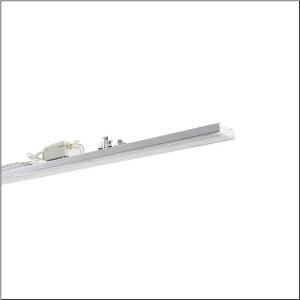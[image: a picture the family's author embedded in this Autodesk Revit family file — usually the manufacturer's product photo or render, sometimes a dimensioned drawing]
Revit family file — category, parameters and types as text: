
# Revit family: licross_21_recessed_mo_52te12dn4axg3s
name_source: partatom
category: Lighting Fixtures
units: mm (PartAtom-declared; Revit-internal decimal feet)

## family parameters
Cut with Voids When Loaded = No
Host = Face
Light Source = No
Part Type = Normal
Room Calculation Point = No
Round Connector Dimension = Use Diameter
Shared = No

## types (1)
- --- (1 x LED, 950 lm, 6.7 W, 4000K)
    Apparent Load = 7 VA
    CIE Flux Codes = 72 92 99 100 100
    Color Rendering = 80
    Color Temperature = 4000K
    Default Elevation = 1800 mm
    Description = Licross 21 Recessed MO, luminaire insert, of sheet steel, galvanised, coil coated, white, length: 1.500mm, width: 66mm, height: 67mm, LED rated luminous flux: 10.280lm, light colour: 840, SDCM (Standard Deviation of Colour Matching)MacAdam ≤ 3 SDCM (initial), control gear: DALI 2 (for two DALI lines), with plug, 6-pole, with phase selection, for trunking rail, 14-core, mains connection: 220..240V, AC, 50/60Hz, rated input power: 62W, internal wiring halogen-free, for emergency light function, for trunking rail, 14-core, converter,control gear: single battery element, battery: LiFePO4, 9Ah, primary optical cover: cover, of PMMA, light emission: direct distribution, primary light characteristic: symmetric, protection rating (complete): IP54, insulation class (complete): insulation class I (protective earthing), certification: CE, UKCA, protection symbol: D if used in an environment with non-conductive dust loads with corresponding accessories, impact resistance: IK06, permissible ambient temperature for indoor applications: +5..+35°C, standard: EN 60598-2-22, LABS conformity tested according to VDMA 24364:2018-05, reducing of maximum allowable ambient temperature of 5°C with ceiling mounting, corresponds to IFS (International Featured Standards) requirements for safety and quality in the food industry, The light source and the operating device comply with the requirements of the Ecodesign Regulation (EU) 2019/2020 and are replaceable in accordance with this regulation, packaging unit: 1 piece
    Height = 58 mm
    Lamp = 1 x LED
    Lamp Light Flux = 950 lm
    Lamp Power = 6.7 W
    Lamp count = 1
    Length = 1500 mm
    Luminous efficacy = 142 lm/W
    Manufacturer = Siteco
    ModVariant = No
    Model = 52TE12DN4AXG3S
    Mounting Place = Ceiling
    Mounting Type = Pendant
    Number of Poles = 1
    OnlyDefault = Yes
    Power Factor = 1
    Product Name = Licross 21 Recessed MO
    Product group = luminaire insert | ceiling pendant
    ProductGroupID = 901
    Protection Class = Protection class I
    Protection Degree = IP 54
    RLX_Detail_Level = 1
    RLX_Emergency_Light_Flux = 0 lm
    RLX_Emergency_Type = 0
    RLX_Emergency_Type_DB = No
    RlxData = <blob elided: 25297 chars, md5=afd6981c>
    Socket = socket
    Standby Power = 0 W
    System Light Flux = 950 lm
    System Power = 7 W
    Type Comments = : emergency light operation: 3 h
    Type Image = l_1296930.jpg
    URL = http://relux.com
    VarID = @adj_111561
    Voltage = 0 V
    Weight = 0.00 kg
    Width = 66 mm

## geometry (parser evidence)
native form markers: Blend x4, Sweep x11
no freeform markers — native parametric forms only
